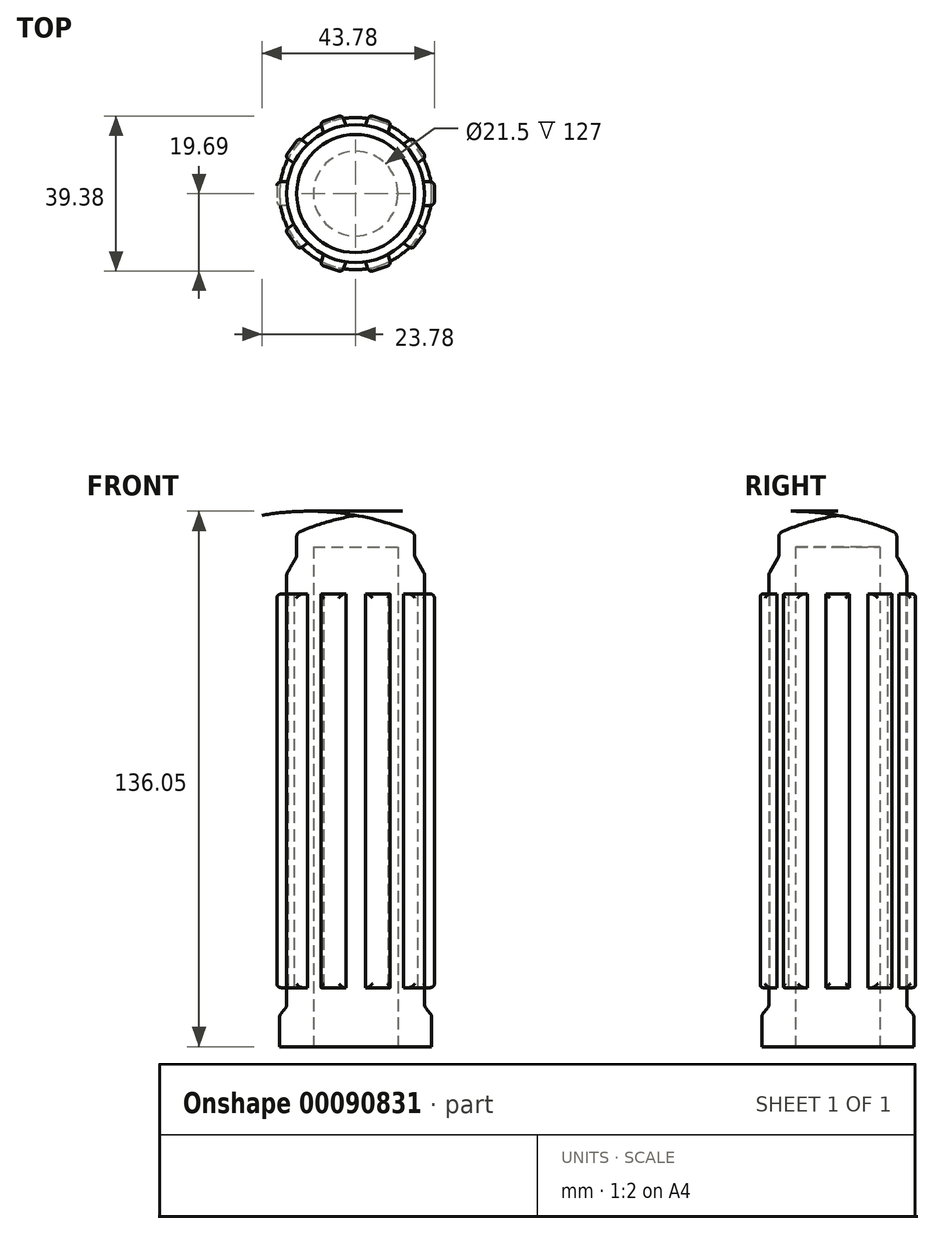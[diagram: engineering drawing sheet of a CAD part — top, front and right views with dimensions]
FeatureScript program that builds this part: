
annotation { "Feature Type Name" : "Feature", "Feature Type Description" : "" }
export const myFeature = defineFeature(function(context is Context, id is Id, definition is map)
    precondition{}
    {
        {
            var Q0;
            Q0=qCreatedBy(makeId("Front.planeOp"),FACE);
            var sketch = newSketch(context, id + "F0", { "sketchPlane" : qUnion([Q0])});
            skLineSegment(sketch, "E0", {"start": v(10.75, 0) * mm, "end": v(10.75, 127) * mm});
            skLineSegment(sketch, "E1", {"start": v(0, 0) * mm, "end": v(0, 170.76) * mm, "construction": true});
            skLineSegment(sketch, "E2", {"start": v(10.75, 127) * mm, "end": v(0, 127) * mm});
            skLineSegment(sketch, "E3", {"start": v(0, 127) * mm, "end": v(0, 135) * mm});
            skLineSegment(sketch, "E4", {"start": v(15, 130.5) * mm, "end": v(15, 124.5) * mm});
            skLineSegment(sketch, "E5", {"start": v(15, 124.5) * mm, "end": v(17.5, 120.17) * mm});
            skLineSegment(sketch, "E6", {"start": v(17.5, 120.17) * mm, "end": v(17.5, 10.17) * mm});
            skLineSegment(sketch, "E7", {"start": v(17.5, 10.17) * mm, "end": v(19.33, 8) * mm});
            skLineSegment(sketch, "E8", {"start": v(19.32, 8) * mm, "end": v(19.32, 0) * mm});
            skLineSegment(sketch, "E9", {"start": v(19.32, 0) * mm, "end": v(10.75, 0) * mm});
            skArc(sketch, "E10", {"start": v(15, 130.5) * mm, "mid": v(7.63, 133.19) * mm, "end": v(0, 135) * mm});
            skSolve(sketch);
        }
        {
            var Q0;
            Q0=makeQuery(id+"F0.imprint","IMPRINT",FACE,{"disambiguationData":[TD([[makeQuery(id+"F0.imprint","IMPRINT",EDGE,{"derivedFrom":sQuery(id+"F0.wireOp",EDGE,"E0")}),-1.0]])]});
            var Q1;
            Q1=sQuery(id+"F0.wireOp",EDGE,"E3");
            revolve(context, id + "F1", {"entities" : qUnion([Q0]), "axis" : qUnion([Q1]), "revolveType" : RevolveType.FULL});
        }
        {
            var Q0;
            Q0=makeQuery(id+"F1.opRevolve","SWEPT_EDGE",EDGE,{"disambiguationData":[OSD([sQuery(id+"F0.wireOp",EDGE,"E4"),sQuery(id+"F0.wireOp",EDGE,"E5")])]});
            var Q1;
            Q1=makeQuery(id+"F1.opRevolve","SWEPT_EDGE",EDGE,{"disambiguationData":[OSD([sQuery(id+"F0.wireOp",EDGE,"E4"),sQuery(id+"F0.wireOp",EDGE,"E10")])]});
            var Q2;
            Q2=makeQuery(id+"F1.opRevolve","SWEPT_EDGE",EDGE,{"disambiguationData":[OSD([sQuery(id+"F0.wireOp",EDGE,"E5"),sQuery(id+"F0.wireOp",EDGE,"E6")])]});
            var Q3;
            Q3=makeQuery(id+"F1.opRevolve","SWEPT_EDGE",EDGE,{"disambiguationData":[OSD([sQuery(id+"F0.wireOp",EDGE,"E6"),sQuery(id+"F0.wireOp",EDGE,"E7")])]});
            var Q4;
            Q4=makeQuery(id+"F1.opRevolve","SWEPT_EDGE",EDGE,{"disambiguationData":[OSD([sQuery(id+"F0.wireOp",EDGE,"E7"),sQuery(id+"F0.wireOp",EDGE,"E8")])]});
            fillet(context, id + "F2", {"entities" : qUnion([Q0, Q1, Q2, Q3, Q4]), "radius" : 1.6 * mm, "tangentPropagation" : true, "allowEdgeOverflow" : false});
        }
        {
            var Q0;
            Q0=qCreatedBy(makeId("Right.planeOp"),FACE);
            cPlane(context, id + "F3", {"entities" : qUnion([Q0]), "cplaneType" : CPlaneType.OFFSET, "offset" : 20 * mm, "width" : 150 * mm, "height" : 150 * mm});
        }
        {
            var Q0;
            Q0=qCreatedBy(id+"F3.planeOp",FACE);
            var sketch = newSketch(context, id + "F4", { "sketchPlane" : qUnion([Q0])});
            skLineSegment(sketch, "E11.bottom", {"start": v(-3, 115) * mm, "end": v(3, 115) * mm});
            skLineSegment(sketch, "E11.top", {"start": v(-3, 15) * mm, "end": v(3, 15) * mm});
            skLineSegment(sketch, "E11.left", {"start": v(-3, 115) * mm, "end": v(-3, 15) * mm});
            skLineSegment(sketch, "E11.right", {"start": v(3, 115) * mm, "end": v(3, 15) * mm});
            skSolve(sketch);
        }
        {
            var Q0;
            Q0=makeQuery(id+"F4.imprint","IMPRINT",FACE,{"disambiguationData":[TD([[makeQuery(id+"F4.imprint","IMPRINT",EDGE,{"derivedFrom":sQuery(id+"F4.wireOp",EDGE,"E11.bottom")}),-1.0]])]});
            var Q1;
            Q1=makeQuery(id+"F1.opRevolve","SWEPT_FACE",FACE,{"disambiguationData":[OSD([sQuery(id+"F0.wireOp",EDGE,"E6")])]});
            extrude(context, id + "F5", {"entities" : qUnion([Q0]), "endBound" : BoundingType.UP_TO_SURFACE, "oppositeDirection" : true, "endBoundEntityFace" : qUnion([Q1]), "depth" : 25 * mm});
        }
        {
            var Q0;
            Q0=makeQuery(id+"F5.opExtrude","CAP_EDGE",EDGE,{"disambiguationData":[OSD([sQuery(id+"F4.wireOp",EDGE,"E11.right")])],"isStart":true});
            var Q1;
            Q1=makeQuery(id+"F5.opExtrude","CAP_EDGE",EDGE,{"disambiguationData":[OSD([sQuery(id+"F4.wireOp",EDGE,"E11.left")])],"isStart":true});
            var Q2;
            Q2=makeQuery(id+"F5.opExtrude","CAP_EDGE",EDGE,{"disambiguationData":[OSD([sQuery(id+"F4.wireOp",EDGE,"E11.top")])],"isStart":true});
            var Q3;
            Q3=makeQuery(id+"F5.opExtrude","CAP_EDGE",EDGE,{"disambiguationData":[OSD([sQuery(id+"F4.wireOp",EDGE,"E11.bottom")])],"isStart":true});
            fillet(context, id + "F6", {"entities" : qUnion([Q0, Q1, Q2, Q3]), "radius" : 1 * mm, "tangentPropagation" : true, "allowEdgeOverflow" : false});
        }
        {
            var Q0;
            Q0=makeQuery(id+"F5.opExtrude","SWEPT_BODY",BODY,{"disambiguationData":[OSD([sQuery(id+"F4.wireOp",EDGE,"E11.bottom"),sQuery(id+"F4.wireOp",EDGE,"E11.top"),sQuery(id+"F4.wireOp",EDGE,"E11.left"),sQuery(id+"F4.wireOp",EDGE,"E11.right")])]});
            var Q1;
            Q1=makeQuery(id+"F1.opRevolve","SWEPT_FACE",FACE,{"disambiguationData":[OSD([sQuery(id+"F0.wireOp",EDGE,"E6")])]});
            circularPattern(context, id + "F7", {"entities" : qUnion([Q0]), "axis" : qUnion([Q1]), "angle" : 360 * degree, "instanceCount" : 10, "oppositeDirection" : true, "equalSpace" : true});
        }
    });
